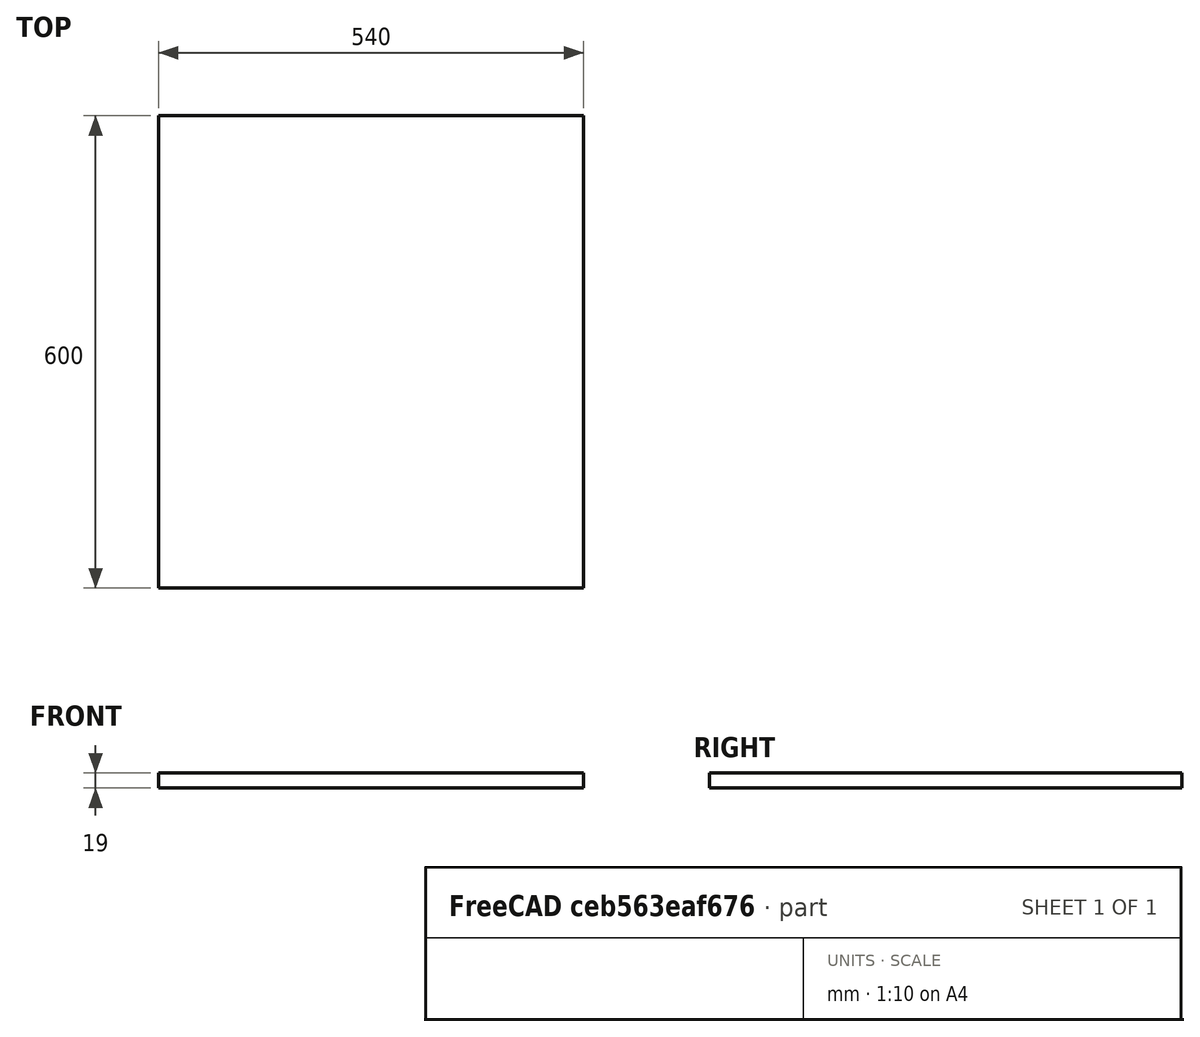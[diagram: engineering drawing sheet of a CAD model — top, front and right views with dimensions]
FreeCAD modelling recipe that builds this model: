
FCSTD DOCUMENT  (FreeCAD 1.0RUnknown)
Label: wardrobe_base_jan
License: All rights reserved
LicenseURL: https://en.wikipedia.org/wiki/All_rights_reserved
objects: PartDesign::CoordinateSystem×9, Sketcher::SketchObject×2, PartDesign::Pad×1, PartDesign::Body×1
note: 17 computed .brp shape members not serialized (recipe doc carries the construction recipe); baked Part::Feature solids carry a one-line shape summary decoded from their .brp
EXTERNAL_REF file=../../mastersketch.FCStd obj=Spreadsheet

FEATURE [Sketcher::SketchObject] Sketch
  ArcFitTolerance = 1e-06
  AttachmentSupport = -> [XY_Plane]
  FullyConstrained = true
  MakeInternals = false
  MapMode = 5
  expr: Constraints[10] = mastersketch#Spreadsheet.corpus_width
  expr: Constraints[11] = mastersketch#Spreadsheet.corpus_depth
  sketch-geometry (5):
    g0: LineSegment StartX=-270 StartY=-300 StartZ=0 EndX=270 EndY=-300 EndZ=0
    g1: LineSegment StartX=270 StartY=-300 StartZ=0 EndX=270 EndY=300 EndZ=0
    g2: LineSegment StartX=270 StartY=300 StartZ=0 EndX=-270 EndY=300 EndZ=0
    g3: LineSegment StartX=-270 StartY=300 StartZ=0 EndX=-270 EndY=-300 EndZ=0
    g4: GeomPoint [constr] X=0 Y=0 Z=0
  constraints (12):
    c: Coincident(g0,g1)
    c: Coincident(g1,g2)
    c: Coincident(g2,g3)
    c: Coincident(g3,g0)
    c: Horizontal(g0)
    c: Horizontal(g2)
    c: Vertical(g1)
    c: Vertical(g3)
    c: Symmetric(g2,g0,g4)
    c: Coincident(g4,g-1)
    c: DistanceX(g0,g0) = 540
    c: DistanceY(g3,g3) = 600
FEATURE [PartDesign::Pad] Pad
  Direction = (0,0,1)
  Length = 19
  Length2 = 10
  Profile = -> Sketch
  ReferenceAxis = -> Sketch [N_Axis]
  Refine = true
  Suppressed = false
  Type = 0
  expr: Length = mastersketch#Spreadsheet.corpus_outer_thickness
FEATURE [PartDesign::CoordinateSystem] LCS_1  label="LCS_left"
  AttacherType = Attacher::AttachEngine3D
  AttachmentSupport = -> [Pad]
  MapMode = 45
  Placement = pos=(-270,1.42e-14,19) rot=(0,0.707107,0.707107;3.14159rad)
FEATURE [PartDesign::CoordinateSystem] LCS_right  label="LCS-right"
  AttacherType = Attacher::AttachEngine3D
  AttachmentSupport = -> [Pad]
  MapMode = 45
  Placement = pos=(270,-1.42e-14,19) rot=(0,0.707107,0.707107;3.14159rad)
FEATURE [PartDesign::CoordinateSystem] LCS_center
  AttacherType = Attacher::AttachEngine3D
FEATURE [Sketcher::SketchObject] Sketch_1  label="feet_placement"
  ArcFitTolerance = 1e-06
  AttachmentSupport = -> [Pad]
  FullyConstrained = true
  MakeInternals = false
  MapMode = 5
  Placement = pos=(0,0,0) rot=(1,0,0;3.14159rad)
  expr: Constraints[10] = mastersketch#Spreadsheet.corpus_width - 100
  expr: Constraints[11] = mastersketch#Spreadsheet.corpus_depth - 140
  sketch-geometry (5):
    g0: LineSegment StartX=-220 StartY=-230 StartZ=0 EndX=220 EndY=-230 EndZ=0
    g1: LineSegment StartX=220 StartY=-230 StartZ=0 EndX=220 EndY=230 EndZ=0
    g2: LineSegment StartX=220 StartY=230 StartZ=0 EndX=-220 EndY=230 EndZ=0
    g3: LineSegment StartX=-220 StartY=230 StartZ=0 EndX=-220 EndY=-230 EndZ=0
    g4: GeomPoint [constr] X=0 Y=0 Z=0
  constraints (12):
    c: Coincident(g0,g1)
    c: Coincident(g1,g2)
    c: Coincident(g2,g3)
    c: Coincident(g3,g0)
    c: Horizontal(g0)
    c: Horizontal(g2)
    c: Vertical(g1)
    c: Vertical(g3)
    c: Symmetric(g2,g0,g4)
    c: Coincident(g4,g-1)
    c: DistanceX(g0,g0) = 440
    c: DistanceY(g3,g3) = 460
FEATURE [PartDesign::CoordinateSystem] LCS_2  label="LCS_feet0"
  AttacherType = Attacher::AttachEngine3D
  AttachmentSupport = -> [Sketch_1]
  MapMode = 1
  Placement = pos=(-220,-230,0) rot=(0,0,1;0rad)
FEATURE [PartDesign::CoordinateSystem] LCS_feet1
  AttacherType = Attacher::AttachEngine3D
  AttachmentSupport = -> [Sketch_1]
  MapMode = 1
  Placement = pos=(220,-230,0) rot=(0,0,1;0rad)
FEATURE [PartDesign::CoordinateSystem] LCS_feet2
  AttacherType = Attacher::AttachEngine3D
  AttachmentSupport = -> [Sketch_1]
  MapMode = 1
  Placement = pos=(220,230,0) rot=(0,0,1;0rad)
FEATURE [PartDesign::CoordinateSystem] LCS_feet3
  AttacherType = Attacher::AttachEngine3D
  AttachmentSupport = -> [Sketch_1]
  MapMode = 1
  Placement = pos=(-220,230,0) rot=(0,0,1;0rad)
FEATURE [PartDesign::CoordinateSystem] LCS_back
  AttacherType = Attacher::AttachEngine3D
  AttachmentSupport = -> [Pad]
  MapMode = 45
  Placement = pos=(0,300,0) rot=(0.57735,0.57735,0.57735;2.0944rad)
FEATURE [PartDesign::CoordinateSystem] LCS_door
  AttacherType = Attacher::AttachEngine3D
  AttachmentSupport = -> [Pad]
  MapMode = 7
  Placement = pos=(270,-300,0) rot=(0,1,0;3.14159rad)
FEATURE [PartDesign::Body] Body  label="wardrobe_base_jan"
  AllowCompound = false
  Group = -> [Sketch,Pad,LCS_1,LCS_right,LCS_center,Sketch_1,LCS_2,LCS_feet1,LCS_feet2,LCS_feet3,LCS_back,LCS_door]
  Origin = -> Origin
  Tip = -> Pad
